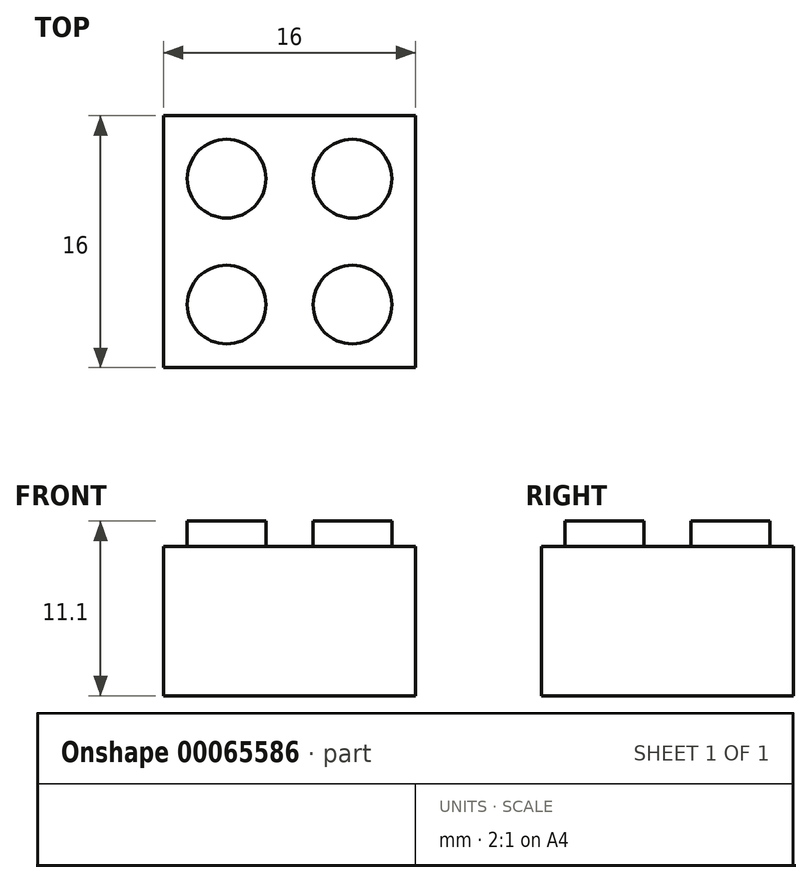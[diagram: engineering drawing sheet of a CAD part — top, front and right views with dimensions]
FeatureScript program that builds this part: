
annotation { "Feature Type Name" : "Feature", "Feature Type Description" : "" }
export const myFeature = defineFeature(function(context is Context, id is Id, definition is map)
    precondition{}
    {
        {
            var Q0;
            Q0=qCreatedBy(makeId("Top.planeOp"),FACE);
            var sketch = newSketch(context, id + "F0", { "sketchPlane" : qUnion([Q0])});
            skLineSegment(sketch, "E0.rect.bottom", {"start": v(-8, 8) * mm, "end": v(8, 8) * mm});
            skLineSegment(sketch, "E0.rect.top", {"start": v(-8, -8) * mm, "end": v(8, -8) * mm});
            skLineSegment(sketch, "E0.rect.left", {"start": v(-8, 8) * mm, "end": v(-8, -8) * mm});
            skLineSegment(sketch, "E0.rect.right", {"start": v(8, 8) * mm, "end": v(8, -8) * mm});
            skPoint(sketch, "E0.rect.middle", {"position": v(0, 0) * mm});
            skSolve(sketch);
        }
        {
            var Q0;
            Q0 = qSketchRegion(id + "F0", true);
            extrude(context, id + "F1", {"entities" : qUnion([Q0]), "depth" : 9.5 * mm});
        }
        {
            var Q0;
            Q0=makeQuery(id+"F1.opExtrude","CAP_FACE",FACE,{"disambiguationData":[OSD([sQuery(id+"F0.wireOp",EDGE,"E0.rect.bottom"),sQuery(id+"F0.wireOp",EDGE,"E0.rect.top"),sQuery(id+"F0.wireOp",EDGE,"E0.rect.left"),sQuery(id+"F0.wireOp",EDGE,"E0.rect.right")])],"isStart":false});
            var sketch = newSketch(context, id + "F2", { "sketchPlane" : qUnion([Q0])});
            skPoint(sketch, "E1.rect.middle", {"position": v(0, 0) * mm});
            skCircle(sketch, "E2", {"center": v(-4, 4) * mm, "radius": 2.5 * mm});
            skCircle(sketch, "E3", {"center": v(4, -4) * mm, "radius": 2.5 * mm});
            skCircle(sketch, "E4", {"center": v(4, 4) * mm, "radius": 2.5 * mm});
            skCircle(sketch, "E5", {"center": v(-4, -4) * mm, "radius": 2.5 * mm});
            skSolve(sketch);
        }
        {
            var Q0;
            Q0 = qSketchRegion(id + "F2", true);
            extrude(context, id + "F3", {"entities" : qUnion([Q0]), "operationType" : NewBodyOperationType.ADD, "depth" : 1.6 * mm});
        }
    });
